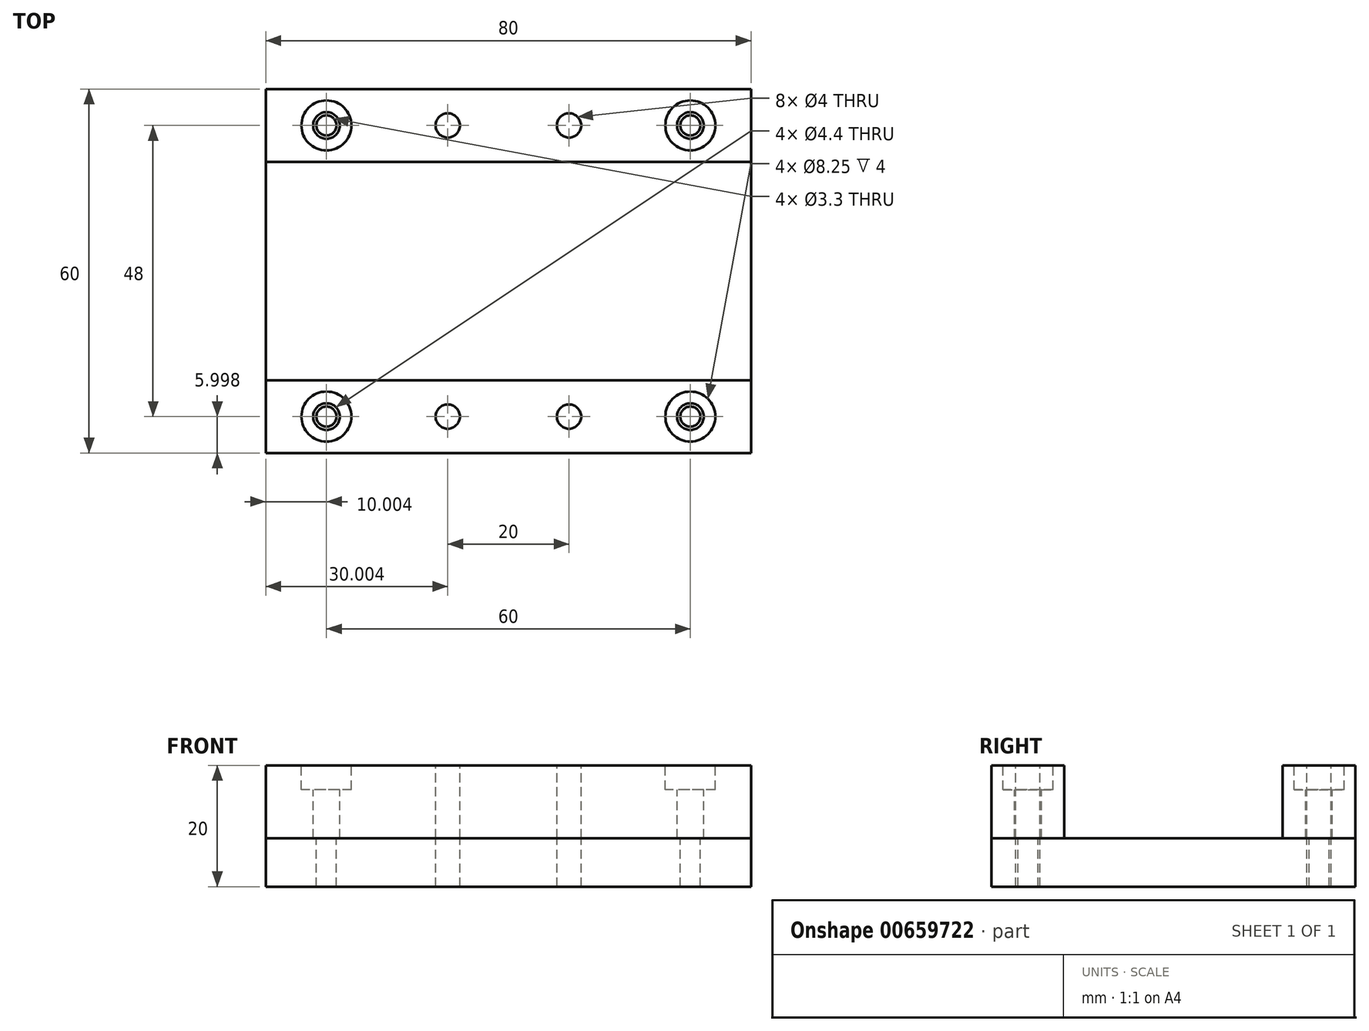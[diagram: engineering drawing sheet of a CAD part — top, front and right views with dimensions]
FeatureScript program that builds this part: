
annotation { "Feature Type Name" : "Feature", "Feature Type Description" : "" }
export const myFeature = defineFeature(function(context is Context, id is Id, definition is map)
    precondition{}
    {
        {
            var Q0;
            Q0=qCreatedBy(makeId("Top.planeOp"),FACE);
            var sketch = newSketch(context, id + "F0", { "sketchPlane" : qUnion([Q0])});
            skLineSegment(sketch, "E0.bottom", {"start": v(-31.85, 34.57) * mm, "end": v(48.15, 34.57) * mm});
            skLineSegment(sketch, "E0.top", {"start": v(-31.85, -25.43) * mm, "end": v(48.15, -25.43) * mm});
            skLineSegment(sketch, "E0.left", {"start": v(-31.85, 34.57) * mm, "end": v(-31.85, -25.43) * mm});
            skLineSegment(sketch, "E0.right", {"start": v(48.15, 34.57) * mm, "end": v(48.15, -25.43) * mm});
            skSolve(sketch);
        }
        {
            var Q0;
            Q0=makeQuery(id+"F0.imprint","IMPRINT",FACE,{"disambiguationData":[TD([[makeQuery(id+"F0.imprint","IMPRINT",EDGE,{"derivedFrom":sQuery(id+"F0.wireOp",EDGE,"E0.bottom")}),-1.0]])]});
            extrude(context, id + "F1", {"entities" : qUnion([Q0]), "depth" : 8 * mm, "offsetDistance" : 25 * mm});
        }
        {
            var Q0;
            Q0=makeQuery(id+"F1.opExtrude","CAP_FACE",FACE,{"disambiguationData":[OSD([sQuery(id+"F0.wireOp",EDGE,"E0.bottom"),sQuery(id+"F0.wireOp",EDGE,"E0.top"),sQuery(id+"F0.wireOp",EDGE,"E0.left"),sQuery(id+"F0.wireOp",EDGE,"E0.right")])],"isStart":false});
            var sketch = newSketch(context, id + "F2", { "sketchPlane" : qUnion([Q0])});
            skLineSegment(sketch, "E1.bottom", {"start": v(-31.85, 34.57) * mm, "end": v(48.15, 34.57) * mm});
            skLineSegment(sketch, "E1.top", {"start": v(-31.85, 22.57) * mm, "end": v(48.15, 22.57) * mm});
            skLineSegment(sketch, "E1.left", {"start": v(-31.85, 34.57) * mm, "end": v(-31.85, 22.57) * mm});
            skLineSegment(sketch, "E1.right", {"start": v(48.15, 34.57) * mm, "end": v(48.15, 22.57) * mm});
            skLineSegment(sketch, "E2.bottom", {"start": v(-31.85, -25.43) * mm, "end": v(48.15, -25.43) * mm});
            skLineSegment(sketch, "E2.top", {"start": v(-31.85, -13.43) * mm, "end": v(48.15, -13.43) * mm});
            skLineSegment(sketch, "E2.left", {"start": v(-31.85, -25.43) * mm, "end": v(-31.85, -13.43) * mm});
            skLineSegment(sketch, "E2.right", {"start": v(48.15, -25.43) * mm, "end": v(48.15, -13.43) * mm});
            skSolve(sketch);
        }
        {
            var Q0;
            Q0=makeQuery(id+"F2.imprint","IMPRINT",FACE,{"disambiguationData":[TD([[makeQuery(id+"F2.imprint","IMPRINT",EDGE,{"derivedFrom":sQuery(id+"F2.wireOp",EDGE,"E1.bottom")}),-1.0]])]});
            var Q1;
            Q1=makeQuery(id+"F2.imprint","IMPRINT",FACE,{"disambiguationData":[TD([[makeQuery(id+"F2.imprint","IMPRINT",EDGE,{"derivedFrom":sQuery(id+"F2.wireOp",EDGE,"E2.bottom")}),1.0]])]});
            extrude(context, id + "F3", {"entities" : qUnion([Q0, Q1]), "depth" : 12 * mm, "offsetDistance" : 25 * mm});
        }
        {
            var Q0;
            Q0=makeQuery(id+"F3.opExtrude","CAP_FACE",FACE,{"disambiguationData":[OSD([sQuery(id+"F2.wireOp",EDGE,"E1.bottom"),sQuery(id+"F2.wireOp",EDGE,"E1.top"),sQuery(id+"F2.wireOp",EDGE,"E1.left"),sQuery(id+"F2.wireOp",EDGE,"E1.right")])],"isStart":false});
            var sketch = newSketch(context, id + "F4", { "sketchPlane" : qUnion([Q0])});
            skPoint(sketch, "E3", {"position": v(-59.9, 52.87) * mm});
            skPoint(sketch, "E4", {"position": v(80.5, 52.87) * mm});
            skPoint(sketch, "E5", {"position": v(80.5, -46.78) * mm});
            skPoint(sketch, "E6", {"position": v(-59.9, -48.34) * mm});
            skPoint(sketch, "E7", {"position": v(-21.85, 28.57) * mm});
            skLineSegment(sketch, "E8", {"start": v(-31.85, -25.43) * mm, "end": v(48.15, 34.57) * mm});
            skLineSegment(sketch, "E9", {"start": v(-31.85, 34.57) * mm, "end": v(48.15, -25.43) * mm});
            skLineSegment(sketch, "E10", {"start": v(8.15, 4.57) * mm, "end": v(47.76, 4.57) * mm});
            skLineSegment(sketch, "E11", {"start": v(47.76, 4.57) * mm, "end": v(-31.8, 4.57) * mm});
            skLineSegment(sketch, "E12", {"start": v(8.15, 4.57) * mm, "end": v(8.15, 34.57) * mm});
            skLineSegment(sketch, "E13", {"start": v(8.15, 34.57) * mm, "end": v(8.15, -24.98) * mm});
            skLineSegment(sketch, "E14.MirrorCS", {"start": v(8.15, -25.43) * mm, "end": v(8.15, 34.12) * mm});
            skPoint(sketch, "E15.MirrorP", {"position": v(-21.85, -19.43) * mm});
            skPoint(sketch, "E16.MirrorP", {"position": v(38.15, 28.57) * mm});
            skLineSegment(sketch, "E17.MirrorCS", {"start": v(-31.45, 4.57) * mm, "end": v(48.11, 4.57) * mm});
            skPoint(sketch, "E18.MirrorP", {"position": v(38.15, -19.43) * mm});
            skPoint(sketch, "E19", {"position": v(-1.85, 28.41) * mm});
            skPoint(sketch, "E20", {"position": v(-31.85, 28.41) * mm});
            skPoint(sketch, "E21", {"position": v(-1.85, -19.1) * mm});
            skPoint(sketch, "E22", {"position": v(18.15, 28.54) * mm});
            skPoint(sketch, "E23", {"position": v(18.15, -19.1) * mm});
            skSolve(sketch);
        }
        {
            var Q0;
            Q0=sQuery(id+"F4.wireOp",VERTEX,"E7");
            var Q1;
            Q1=sQuery(id+"F4.wireOp",VERTEX,"E16.MirrorP");
            var Q2;
            Q2=sQuery(id+"F4.wireOp",VERTEX,"E18.MirrorP");
            var Q3;
            Q3=sQuery(id+"F4.wireOp",VERTEX,"E15.MirrorP");
            var Q4;
            Q4=makeQuery(id+"F3.opExtrude","SWEPT_BODY",BODY,{"disambiguationData":[OSD([sQuery(id+"F2.wireOp",EDGE,"E1.bottom"),sQuery(id+"F2.wireOp",EDGE,"E1.top"),sQuery(id+"F2.wireOp",EDGE,"E1.left"),sQuery(id+"F2.wireOp",EDGE,"E1.right")])]});
            var Q5;
            Q5=makeQuery(id+"F3.opExtrude","SWEPT_BODY",BODY,{"disambiguationData":[OSD([sQuery(id+"F2.wireOp",EDGE,"E2.bottom"),sQuery(id+"F2.wireOp",EDGE,"E2.top"),sQuery(id+"F2.wireOp",EDGE,"E2.left"),sQuery(id+"F2.wireOp",EDGE,"E2.right")])]});
            hole(context, id + "F5", {"style" : HoleStyle.C_BORE, "endStyle" : HoleEndStyle.BLIND, "standardTappedOrClearance" : lookupTablePath({ "standard" : "ISO", "fit" : "Normal", "size" : "M4", "type" : "Clearance" }), "standardBlindInLast" : lookupTablePath({ "fit" : "Standard", "standard" : "ISO", "size" : "M4", "type" : "Clearance" }), "holeDiameter" : 4.4 * mm, "cBoreDiameter" : 8.25 * mm, "cBoreDepth" : 4 * mm, "majorDiameter" : 5 * mm, "holeDepth" : 12 * mm, "isTappedThrough" : true, "tappedDepth" : 12 * mm, "tapClearance" : 3, "startFromSketch" : true, "locations" : qUnion([Q0, Q1, Q2, Q3]), "scope" : qUnion([Q4, Q5])});
        }
        {
            var Q0;
            Q0=makeQuery(id+"F3.opExtrude","CAP_FACE",FACE,{"disambiguationData":[OSD([sQuery(id+"F2.wireOp",EDGE,"E1.bottom"),sQuery(id+"F2.wireOp",EDGE,"E1.top"),sQuery(id+"F2.wireOp",EDGE,"E1.left"),sQuery(id+"F2.wireOp",EDGE,"E1.right")])],"isStart":false});
            var sketch = newSketch(context, id + "F6", { "sketchPlane" : qUnion([Q0])});
            skPoint(sketch, "E24", {"position": v(-1.85, 28.57) * mm});
            skPoint(sketch, "E25", {"position": v(18.15, 28.57) * mm});
            skPoint(sketch, "E26", {"position": v(-1.85, -19.43) * mm});
            skPoint(sketch, "E27", {"position": v(18.15, -19.43) * mm});
            skSolve(sketch);
        }
        {
            var Q0;
            Q0=sQuery(id+"F6.wireOp",VERTEX,"E24");
            var Q1;
            Q1=sQuery(id+"F6.wireOp",VERTEX,"E25");
            var Q2;
            Q2=sQuery(id+"F6.wireOp",VERTEX,"E27");
            var Q3;
            Q3=sQuery(id+"F6.wireOp",VERTEX,"E26");
            var Q4;
            Q4=makeQuery(id+"F1.opExtrude","SWEPT_BODY",BODY,{"disambiguationData":[OSD([sQuery(id+"F0.wireOp",EDGE,"E0.bottom"),sQuery(id+"F0.wireOp",EDGE,"E0.top"),sQuery(id+"F0.wireOp",EDGE,"E0.left"),sQuery(id+"F0.wireOp",EDGE,"E0.right")])]});
            var Q5;
            Q5=makeQuery(id+"F3.opExtrude","SWEPT_BODY",BODY,{"disambiguationData":[OSD([sQuery(id+"F2.wireOp",EDGE,"E1.bottom"),sQuery(id+"F2.wireOp",EDGE,"E1.top"),sQuery(id+"F2.wireOp",EDGE,"E1.left"),sQuery(id+"F2.wireOp",EDGE,"E1.right")])]});
            var Q6;
            Q6=makeQuery(id+"F3.opExtrude","SWEPT_BODY",BODY,{"disambiguationData":[OSD([sQuery(id+"F2.wireOp",EDGE,"E2.bottom"),sQuery(id+"F2.wireOp",EDGE,"E2.top"),sQuery(id+"F2.wireOp",EDGE,"E2.left"),sQuery(id+"F2.wireOp",EDGE,"E2.right")])]});
            hole(context, id + "F7", {"style" : HoleStyle.SIMPLE, "endStyle" : HoleEndStyle.THROUGH, "holeDiameter" : 4 * mm, "majorDiameter" : 4 * mm, "isTappedThrough" : true, "tappedDepth" : 12 * mm, "tapClearance" : 3, "startFromSketch" : true, "locations" : qUnion([Q0, Q1, Q2, Q3]), "scope" : qUnion([Q4, Q5, Q6])});
        }
        {
            var Q0;
            Q0=sQuery(id+"F4.wireOp",VERTEX,"E7");
            var Q1;
            Q1=sQuery(id+"F4.wireOp",VERTEX,"E16.MirrorP");
            var Q2;
            Q2=sQuery(id+"F4.wireOp",VERTEX,"E18.MirrorP");
            var Q3;
            Q3=sQuery(id+"F4.wireOp",VERTEX,"E15.MirrorP");
            var Q4;
            Q4=makeQuery(id+"F1.opExtrude","SWEPT_BODY",BODY,{"disambiguationData":[OSD([sQuery(id+"F0.wireOp",EDGE,"E0.bottom"),sQuery(id+"F0.wireOp",EDGE,"E0.top"),sQuery(id+"F0.wireOp",EDGE,"E0.left"),sQuery(id+"F0.wireOp",EDGE,"E0.right")])]});
            hole(context, id + "F8", {"style" : HoleStyle.C_BORE, "endStyle" : HoleEndStyle.THROUGH, "standardTappedOrClearance" : lookupTablePath({ "standard" : "ISO", "engagement" : "75%", "pitch" : "0.7 mm", "size" : "M4", "type" : "Tapped" }), "standardBlindInLast" : lookupTablePath({ "standard" : "ISO", "engagement" : "75%", "pitch" : "0.7 mm", "size" : "M4", "type" : "Tapped" }), "holeDiameter" : 3.3 * mm, "cBoreDiameter" : 8.25 * mm, "cBoreDepth" : 4 * mm, "majorDiameter" : 4 * mm, "showTappedDepth" : true, "isTappedThrough" : true, "tappedDepth" : 12 * mm, "tapClearance" : 3, "startFromSketch" : true, "locations" : qUnion([Q0, Q1, Q2, Q3]), "scope" : qUnion([Q4])});
        }
    });
